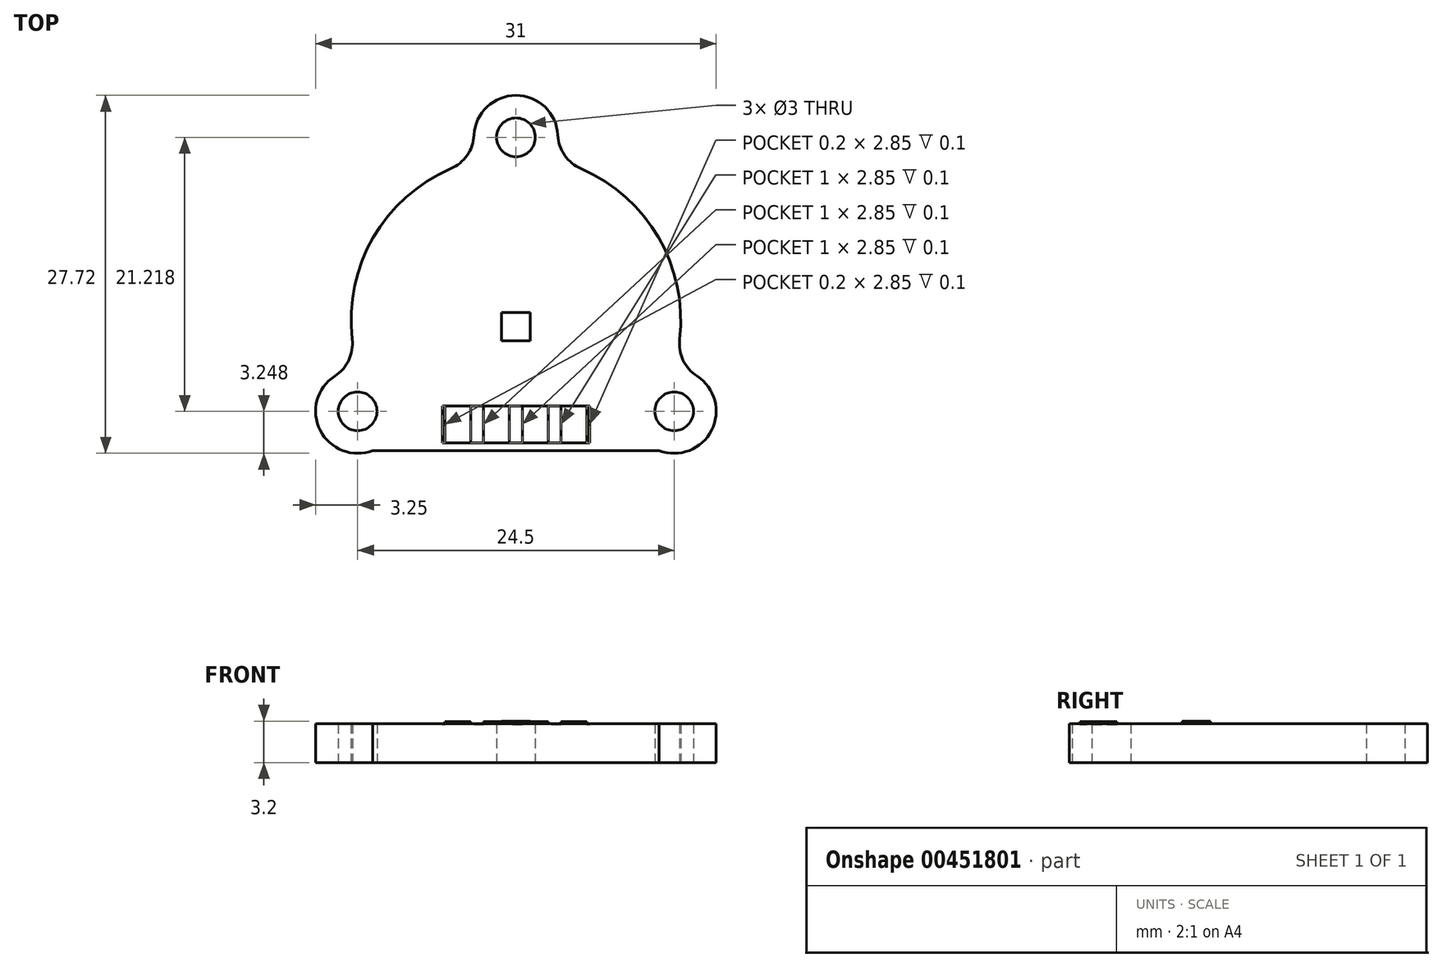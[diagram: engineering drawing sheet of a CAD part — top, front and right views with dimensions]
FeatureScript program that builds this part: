
annotation { "Feature Type Name" : "Feature", "Feature Type Description" : "" }
export const myFeature = defineFeature(function(context is Context, id is Id, definition is map)
    precondition{}
    {
        {
            var Q0;
            Q0=qCreatedBy(makeId("Top.planeOp"),FACE);
            var sketch = newSketch(context, id + "F0", { "sketchPlane" : qUnion([Q0])});
            skPoint(sketch, "E0.0.midPoint", {"position": v(6.13, 3.54) * mm});
            skArc(sketch, "E1", {"start": v(3.25, 14.31) * mm, "mid": v(0, 17.4) * mm, "end": v(-3.25, 14.31) * mm});
            skArc(sketch, "E2", {"start": v(-14.02, -4.35) * mm, "mid": v(-15.15, -8.55) * mm, "end": v(-11.08, -10.1) * mm});
            skArc(sketch, "E3", {"start": v(11.08, -10.1) * mm, "mid": v(15.15, -8.55) * mm, "end": v(14.02, -4.35) * mm});
            skLineSegment(sketch, "E4", {"start": v(-11.08, -10.1) * mm, "end": v(-6.71, -10.1) * mm});
            skLineSegment(sketch, "E5.trimOffspring", {"start": v(7.57, -10.1) * mm, "end": v(11.08, -10.1) * mm});
            skPoint(sketch, "E6.visualSharp", {"position": v(-2.77, 12.45) * mm});
            skArc(sketch, "E6.filletArc", {"start": v(-5.05, 11.71) * mm, "mid": v(-3.78, 12.75) * mm, "end": v(-3.25, 14.31) * mm});
            skPoint(sketch, "E7.visualSharp", {"position": v(2.77, 12.45) * mm});
            skArc(sketch, "E7.filletArc", {"start": v(3.25, 14.31) * mm, "mid": v(3.78, 12.75) * mm, "end": v(5.05, 11.71) * mm});
            skPoint(sketch, "E8.visualSharp", {"position": v(12.17, -3.82) * mm});
            skArc(sketch, "E8.filletArc", {"start": v(12.67, -1.48) * mm, "mid": v(12.93, -3.1) * mm, "end": v(14.02, -4.35) * mm});
            skPoint(sketch, "E9.visualSharp", {"position": v(-12.17, -3.82) * mm});
            skArc(sketch, "E9.filletArc", {"start": v(-14.02, -4.35) * mm, "mid": v(-12.93, -3.1) * mm, "end": v(-12.67, -1.48) * mm});
            skCircle(sketch, "E10", {"center": v(0, 14.15) * mm, "radius": 1.5 * mm});
            skCircle(sketch, "E11", {"center": v(-12.25, -7.07) * mm, "radius": 1.5 * mm});
            skCircle(sketch, "E12", {"center": v(12.25, -7.07) * mm, "radius": 1.5 * mm});
            skArc(sketch, "E13", {"start": v(12.67, -1.48) * mm, "mid": v(11.05, 6.38) * mm, "end": v(5.05, 11.71) * mm});
            skLineSegment(sketch, "E14", {"start": v(7.57, -10.1) * mm, "end": v(-6.71, -10.1) * mm});
            skArc(sketch, "E15.trimOffspring", {"start": v(-5.05, 11.71) * mm, "mid": v(-11.05, 6.38) * mm, "end": v(-12.67, -1.48) * mm});
            skSolve(sketch);
        }
        {
            var Q0;
            Q0 = qSketchRegion(id + "F0", true);
            extrude(context, id + "F1", {"entities" : qUnion([Q0]), "depth" : 3 * mm, "offsetDistance" : 25 * mm});
        }
        {
            var Q0;
            Q0=makeQuery(id+"F1.opExtrude","CAP_FACE",FACE,{"disambiguationData":[OSD([sQuery(id+"F0.wireOp",EDGE,"C7QRfPFi-vLwI-X6gj-dWor-JbQLZ58fUFdR"),sQuery(id+"F0.wireOp",EDGE,"yMvEykNg-osCq-zqkn-151P-fJv8dIBG2HYN"),sQuery(id+"F0.wireOp",EDGE,"E1"),sQuery(id+"F0.wireOp",EDGE,"E2"),sQuery(id+"F0.wireOp",EDGE,"E3"),sQuery(id+"F0.wireOp",EDGE,"e72fb2e6-fbc5-47df-a29e-faecbfe39cbd.trimOffspring"),sQuery(id+"F0.wireOp",EDGE,"E4"),sQuery(id+"F0.wireOp",EDGE,"E5.trimOffspring"),sQuery(id+"F0.wireOp",EDGE,"E6.filletArc"),sQuery(id+"F0.wireOp",EDGE,"E7.filletArc"),sQuery(id+"F0.wireOp",EDGE,"E8.filletArc"),sQuery(id+"F0.wireOp",EDGE,"E9.filletArc"),sQuery(id+"F0.wireOp",EDGE,"E10"),sQuery(id+"F0.wireOp",EDGE,"E11"),sQuery(id+"F0.wireOp",EDGE,"E12")])],"isStart":false});
            var sketch = newSketch(context, id + "F2", { "sketchPlane" : qUnion([Q0])});
            skPoint(sketch, "E16", {"position": v(0, -0.5) * mm});
            skPoint(sketch, "E16.positionSnap0", {"position": v(0, -10.1) * mm});
            skLineSegment(sketch, "E17.bottom", {"start": v(1.1, 0.6) * mm, "end": v(-1.1, 0.6) * mm});
            skLineSegment(sketch, "E17.top", {"start": v(1.1, -1.6) * mm, "end": v(-1.1, -1.6) * mm});
            skLineSegment(sketch, "E17.left", {"start": v(1.1, 0.6) * mm, "end": v(1.1, -1.6) * mm});
            skLineSegment(sketch, "E17.right", {"start": v(-1.1, 0.6) * mm, "end": v(-1.1, -1.6) * mm});
            skSolve(sketch);
        }
        {
            var Q0;
            Q0 = qSketchRegion(id + "F2", true);
            extrude(context, id + "F3", {"entities" : qUnion([Q0]), "operationType" : NewBodyOperationType.ADD, "depth" : 0.2 * mm, "offsetDistance" : 25 * mm});
        }
        {
            var Q0;
            Q0=makeQuery(id+"F1.opExtrude","CAP_FACE",FACE,{"disambiguationData":[OSD([sQuery(id+"F0.wireOp",EDGE,"C7QRfPFi-vLwI-X6gj-dWor-JbQLZ58fUFdR"),sQuery(id+"F0.wireOp",EDGE,"yMvEykNg-osCq-zqkn-151P-fJv8dIBG2HYN"),sQuery(id+"F0.wireOp",EDGE,"E1"),sQuery(id+"F0.wireOp",EDGE,"E2"),sQuery(id+"F0.wireOp",EDGE,"E3"),sQuery(id+"F0.wireOp",EDGE,"e72fb2e6-fbc5-47df-a29e-faecbfe39cbd.trimOffspring"),sQuery(id+"F0.wireOp",EDGE,"E4"),sQuery(id+"F0.wireOp",EDGE,"E5.trimOffspring"),sQuery(id+"F0.wireOp",EDGE,"E6.filletArc"),sQuery(id+"F0.wireOp",EDGE,"E7.filletArc"),sQuery(id+"F0.wireOp",EDGE,"E8.filletArc"),sQuery(id+"F0.wireOp",EDGE,"E9.filletArc"),sQuery(id+"F0.wireOp",EDGE,"E10"),sQuery(id+"F0.wireOp",EDGE,"E11"),sQuery(id+"F0.wireOp",EDGE,"E12")])],"isStart":false});
            var sketch = newSketch(context, id + "F4", { "sketchPlane" : qUnion([Q0])});
            skLineSegment(sketch, "E18.bottom", {"start": v(5.7, -9.5) * mm, "end": v(-5.7, -9.5) * mm});
            skLineSegment(sketch, "E18.top", {"start": v(5.7, -6.65) * mm, "end": v(-5.7, -6.65) * mm});
            skLineSegment(sketch, "E18.left", {"start": v(5.7, -9.5) * mm, "end": v(5.7, -6.65) * mm});
            skLineSegment(sketch, "E18.right", {"start": v(-5.7, -9.5) * mm, "end": v(-5.7, -6.65) * mm});
            skPoint(sketch, "E18.middle", {"position": v(0, -8.08) * mm});
            skPoint(sketch, "E18.middle.positionSnap0", {"position": v(0, -1.6) * mm});
            skPoint(sketch, "E18.centerSnap0", {"position": v(0, -1.6) * mm});
            skPoint(sketch, "E19", {"position": v(0, -0.5) * mm});
            skPoint(sketch, "E19.positionSnap0", {"position": v(-1.1, -0.5) * mm});
            skSolve(sketch);
        }
        {
            var Q0;
            Q0 = qSketchRegion(id + "F4", true);
            extrude(context, id + "F5", {"entities" : qUnion([Q0]), "operationType" : NewBodyOperationType.REMOVE, "oppositeDirection" : true, "depth" : 0.1 * mm, "offsetDistance" : 25 * mm});
        }
        {
            var Q0;
            Q0=makeQuery(id+"F5.boolean.opBoolean","COPY",FACE,{"derivedFrom":makeQuery(id+"F5.opExtrude","CAP_FACE",FACE,{"disambiguationData":[OSD([sQuery(id+"F4.wireOp",EDGE,"E18.bottom"),sQuery(id+"F4.wireOp",EDGE,"E18.top"),sQuery(id+"F4.wireOp",EDGE,"E18.left"),sQuery(id+"F4.wireOp",EDGE,"E18.right")])],"isStart":false})});
            var sketch = newSketch(context, id + "F6", { "sketchPlane" : qUnion([Q0])});
            skLineSegment(sketch, "E20.bottom", {"start": v(-0.5, -6.65) * mm, "end": v(-2.5, -6.65) * mm});
            skLineSegment(sketch, "E20.top", {"start": v(-0.5, -9.5) * mm, "end": v(-2.5, -9.5) * mm});
            skLineSegment(sketch, "E20.left", {"start": v(-0.5, -6.65) * mm, "end": v(-0.5, -9.5) * mm});
            skLineSegment(sketch, "E20.right", {"start": v(-2.5, -6.65) * mm, "end": v(-2.5, -9.5) * mm});
            skLineSegment(sketch, "E21.bottom", {"start": v(-3.5, -6.65) * mm, "end": v(-5.5, -6.65) * mm});
            skLineSegment(sketch, "E21.top", {"start": v(-3.5, -9.5) * mm, "end": v(-5.5, -9.5) * mm});
            skLineSegment(sketch, "E21.left", {"start": v(-3.5, -6.65) * mm, "end": v(-3.5, -9.5) * mm});
            skLineSegment(sketch, "E21.right", {"start": v(-5.5, -6.65) * mm, "end": v(-5.5, -9.5) * mm});
            skLineSegment(sketch, "E22.bottom", {"start": v(0.5, -6.65) * mm, "end": v(2.5, -6.65) * mm});
            skLineSegment(sketch, "E22.top", {"start": v(0.5, -9.5) * mm, "end": v(2.5, -9.5) * mm});
            skLineSegment(sketch, "E22.left", {"start": v(0.5, -6.65) * mm, "end": v(0.5, -9.5) * mm});
            skLineSegment(sketch, "E22.right", {"start": v(2.5, -6.65) * mm, "end": v(2.5, -9.5) * mm});
            skLineSegment(sketch, "E23.bottom", {"start": v(3.5, -6.65) * mm, "end": v(5.5, -6.65) * mm});
            skLineSegment(sketch, "E23.top", {"start": v(3.5, -9.5) * mm, "end": v(5.5, -9.5) * mm});
            skLineSegment(sketch, "E23.left", {"start": v(3.5, -6.65) * mm, "end": v(3.5, -9.5) * mm});
            skLineSegment(sketch, "E23.right", {"start": v(5.5, -6.65) * mm, "end": v(5.5, -9.5) * mm});
            skSolve(sketch);
        }
        {
            var Q0;
            Q0 = qSketchRegion(id + "F6", true);
            extrude(context, id + "F7", {"entities" : qUnion([Q0]), "operationType" : NewBodyOperationType.ADD, "depth" : 0.25 * mm, "offsetDistance" : 25 * mm});
        }
    });
